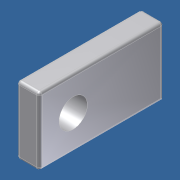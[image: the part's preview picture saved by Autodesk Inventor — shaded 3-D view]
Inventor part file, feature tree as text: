
AUTODESK INVENTOR PART (.ipt)
format: ipt  version: unknown  size: 190,976 bytes
history: native  units: in
note: dims shown in document units (in); Inventor stores cm internally (conversion verified against a paired STEP export)
features: extrude x1, fillet x1, sketch x1
ambient origin geometry x8: Origin, YZ Plane, XZ Plane, XY Plane, X Axis, Y Axis, Z Axis, Center Point
bodies: Solid1 (feature_tree)
feature tree (3):
  extrude  "Extrusion1"  Depth=1.375in
  fillet  "Fillet1"  Radius=0.375in
  sketch  "Sketch1"  dims[d0=0.75in d1=1.375in d4=0.375in d5=0.375in d6=0.3125in d7=0.25in d8=0.0in d9=0.0312in]
